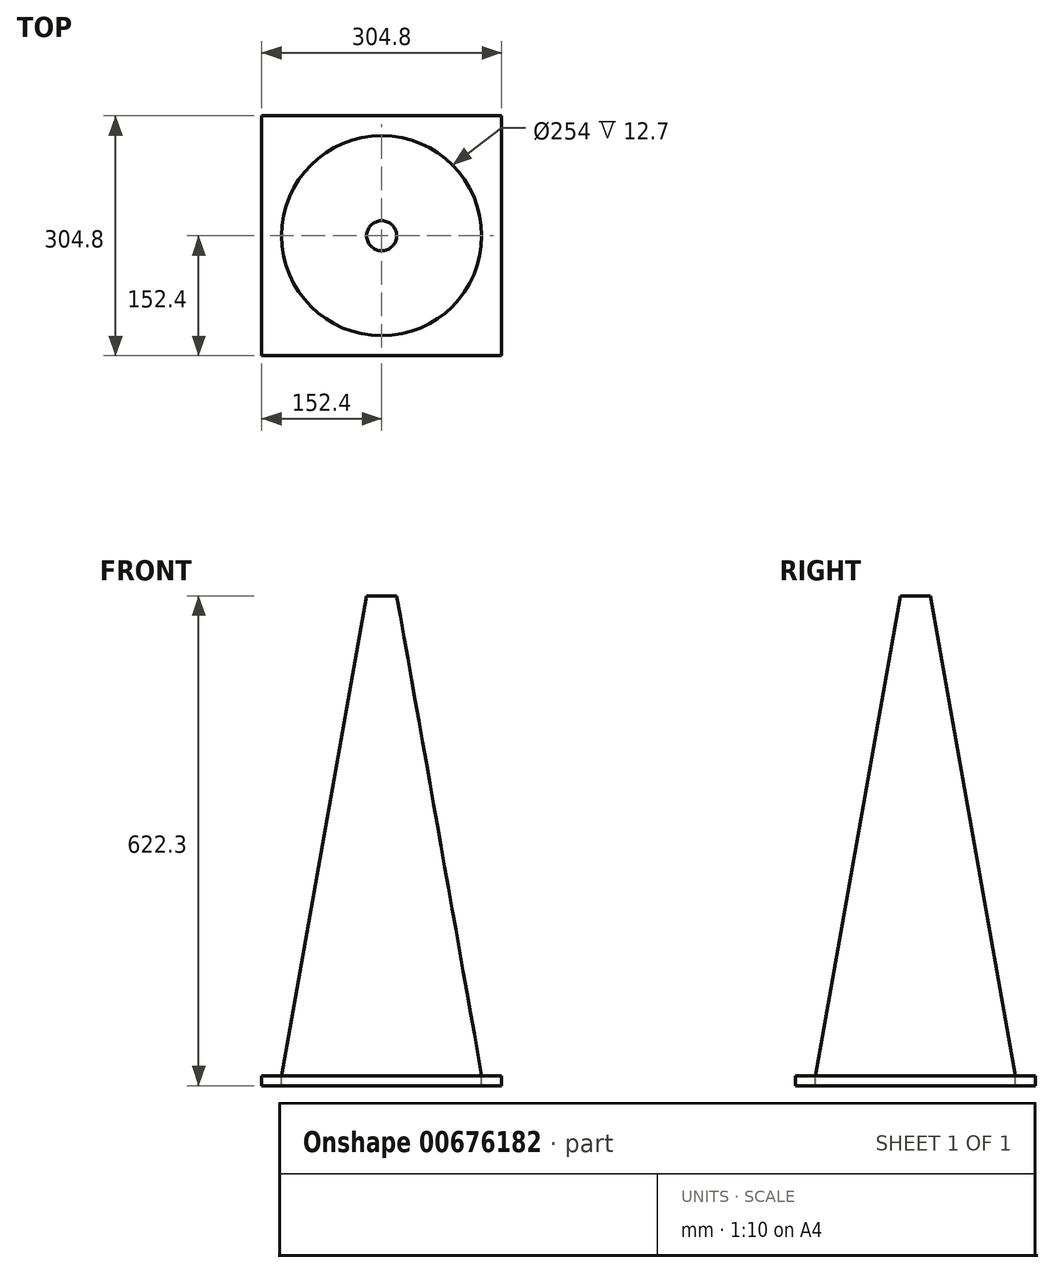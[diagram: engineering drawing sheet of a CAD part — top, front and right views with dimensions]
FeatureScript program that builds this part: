
annotation { "Feature Type Name" : "Feature", "Feature Type Description" : "" }
export const myFeature = defineFeature(function(context is Context, id is Id, definition is map)
    precondition{}
    {
        {
            var Q0;
            Q0=qCreatedBy(makeId("Top.planeOp"),FACE);
            var sketch = newSketch(context, id + "F0", { "sketchPlane" : qUnion([Q0])});
            skCircle(sketch, "E0", {"center": v(0, 0) * mm, "radius": 127 * mm});
            skLineSegment(sketch, "E1.bottom", {"start": v(-152.4, -152.4) * mm, "end": v(152.4, -152.4) * mm});
            skLineSegment(sketch, "E1.top", {"start": v(-152.4, 152.4) * mm, "end": v(152.4, 152.4) * mm});
            skLineSegment(sketch, "E1.left", {"start": v(-152.4, -152.4) * mm, "end": v(-152.4, 152.4) * mm});
            skLineSegment(sketch, "E1.right", {"start": v(152.4, -152.4) * mm, "end": v(152.4, 152.4) * mm});
            skSolve(sketch);
        }
        {
            var Q0;
            Q0=makeQuery(id+"F0.imprint","IMPRINT",FACE,{"disambiguationData":[TD([[makeQuery(id+"F0.imprint","IMPRINT",EDGE,{"derivedFrom":sQuery(id+"F0.wireOp",EDGE,"E0")}),-1.0]])]});
            extrude(context, id + "F1", {"entities" : qUnion([Q0]), "oppositeDirection" : true, "depth" : 12.7 * mm, "offsetDistance" : 25.4 * mm});
        }
        {
            var Q0;
            Q0=makeQuery(id+"F0.imprint","IMPRINT",FACE,{"disambiguationData":[TD([[makeQuery(id+"F0.imprint","IMPRINT",EDGE,{"derivedFrom":sQuery(id+"F0.wireOp",EDGE,"E0")}),-1.0]])]});
            cPlane(context, id + "F2", {"entities" : qUnion([Q0]), "cplaneType" : CPlaneType.OFFSET, "offset" : 609.6 * mm, "width" : 152.4 * mm, "height" : 152.4 * mm});
        }
        {
            var Q0;
            Q0=qCreatedBy(id+"F2.planeOp",FACE);
            var sketch = newSketch(context, id + "F3", { "sketchPlane" : qUnion([Q0])});
            skCircle(sketch, "E2", {"center": v(0, 0) * mm, "radius": 19.05 * mm});
            skSolve(sketch);
        }
        {
            var Q0;
            Q0=makeQuery(id+"F0.imprint","IMPRINT",FACE,{"disambiguationData":[TD([[makeQuery(id+"F0.imprint","IMPRINT",EDGE,{"derivedFrom":sQuery(id+"F0.wireOp",EDGE,"E0")}),1.0]])]});
            var Q1;
            Q1=makeQuery(id+"F3.imprint","IMPRINT",FACE,{"disambiguationData":[TD([[makeQuery(id+"F3.imprint","IMPRINT",EDGE,{"derivedFrom":sQuery(id+"F3.wireOp",EDGE,"E2")}),1.0]])]});
            loft(context, id + "F4", {"sheetProfilesArray" : [{ "sheetProfileEntities" : qUnion([Q0]) }, { "sheetProfileEntities" : qUnion([Q1]) }]});
        }
    });
